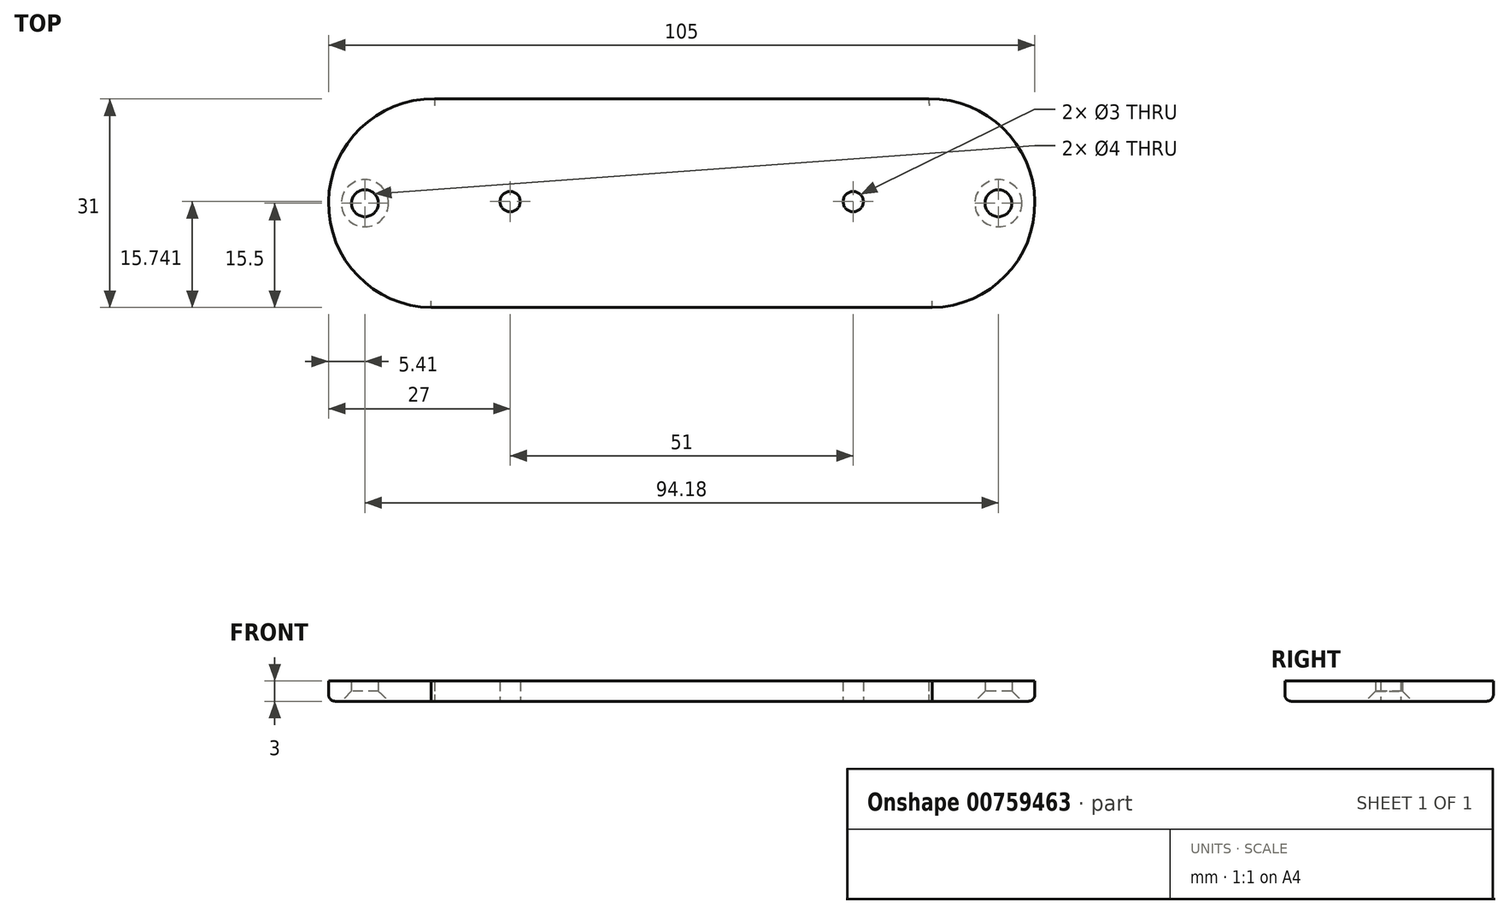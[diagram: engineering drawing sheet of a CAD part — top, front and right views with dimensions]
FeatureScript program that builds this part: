
annotation { "Feature Type Name" : "Feature", "Feature Type Description" : "" }
export const myFeature = defineFeature(function(context is Context, id is Id, definition is map)
    precondition{}
    {
        {
            var Q0;
            Q0=qCreatedBy(makeId("Top.planeOp"),FACE);
            var sketch = newSketch(context, id + "F0", { "sketchPlane" : qUnion([Q0])});
            skPoint(sketch, "E0.middle", {"position": v(0, 0) * mm});
            skArc(sketch, "E1", {"start": v(-36.76, 15.5) * mm, "mid": v(-52.5, 0.24) * mm, "end": v(-37.24, -15.5) * mm});
            skArc(sketch, "E2.MirrorCS", {"start": v(36.76, 15.5) * mm, "mid": v(52.5, 0.24) * mm, "end": v(37.24, -15.5) * mm});
            skCircle(sketch, "E3", {"center": v(-47.1, 0) * mm, "radius": 2 * mm});
            skCircle(sketch, "E4", {"center": v(-25.5, 0.24) * mm, "radius": 1.5 * mm});
            skPoint(sketch, "E4.centerSnap0", {"position": v(-52.5, 0.24) * mm});
            skCircle(sketch, "E5.MirrorC", {"center": v(25.5, 0.24) * mm, "radius": 1.5 * mm});
            skCircle(sketch, "E6.MirrorC", {"center": v(47.1, 0) * mm, "radius": 2 * mm});
            skLineSegment(sketch, "E7", {"start": v(-36.76, 15.5) * mm, "end": v(36.76, 15.5) * mm});
            skLineSegment(sketch, "E8", {"start": v(37.24, -15.5) * mm, "end": v(-37.24, -15.5) * mm});
            skSolve(sketch);
        }
        {
            var Q0;
            Q0 = qSketchRegion(id + "F0", true);
            extrude(context, id + "F1", {"entities" : qUnion([Q0]), "depth" : 3 * mm, "offsetDistance" : 25 * mm});
        }
        {
            var Q0;
            Q0=makeQuery(id+"F1.opExtrude","CAP_EDGE",EDGE,{"disambiguationData":[OSD([sQuery(id+"F0.wireOp",EDGE,"E8")])],"isStart":true});
            var Q1;
            Q1=makeQuery(id+"F1.opExtrude","CAP_EDGE",EDGE,{"disambiguationData":[OSD([sQuery(id+"F0.wireOp",EDGE,"E7")])],"isStart":true});
            var Q2;
            Q2=makeQuery(id+"F1.opExtrude","CAP_EDGE",EDGE,{"disambiguationData":[OSD([sQuery(id+"F0.wireOp",EDGE,"E2.MirrorCS")])],"isStart":true});
            var Q3;
            Q3=makeQuery(id+"F1.opExtrude","CAP_EDGE",EDGE,{"disambiguationData":[OSD([sQuery(id+"F0.wireOp",EDGE,"E1")])],"isStart":true});
            fillet(context, id + "F2", {"entities" : qUnion([Q0, Q1, Q2, Q3]), "radius" : 1 * mm, "tangentPropagation" : true, "allowEdgeOverflow" : false});
        }
        {
            var Q0;
            Q0=makeQuery(id+"F1.opExtrude","CAP_EDGE",EDGE,{"disambiguationData":[OSD([sQuery(id+"F0.wireOp",EDGE,"E3")])],"isStart":true});
            var Q1;
            Q1=makeQuery(id+"F1.opExtrude","CAP_EDGE",EDGE,{"disambiguationData":[OSD([sQuery(id+"F0.wireOp",EDGE,"E6.MirrorC")])],"isStart":true});
            chamfer(context, id + "F3", {"entities" : qUnion([Q0, Q1]), "width" : 1.5 * mm, "tangentPropagation" : true});
        }
    });
